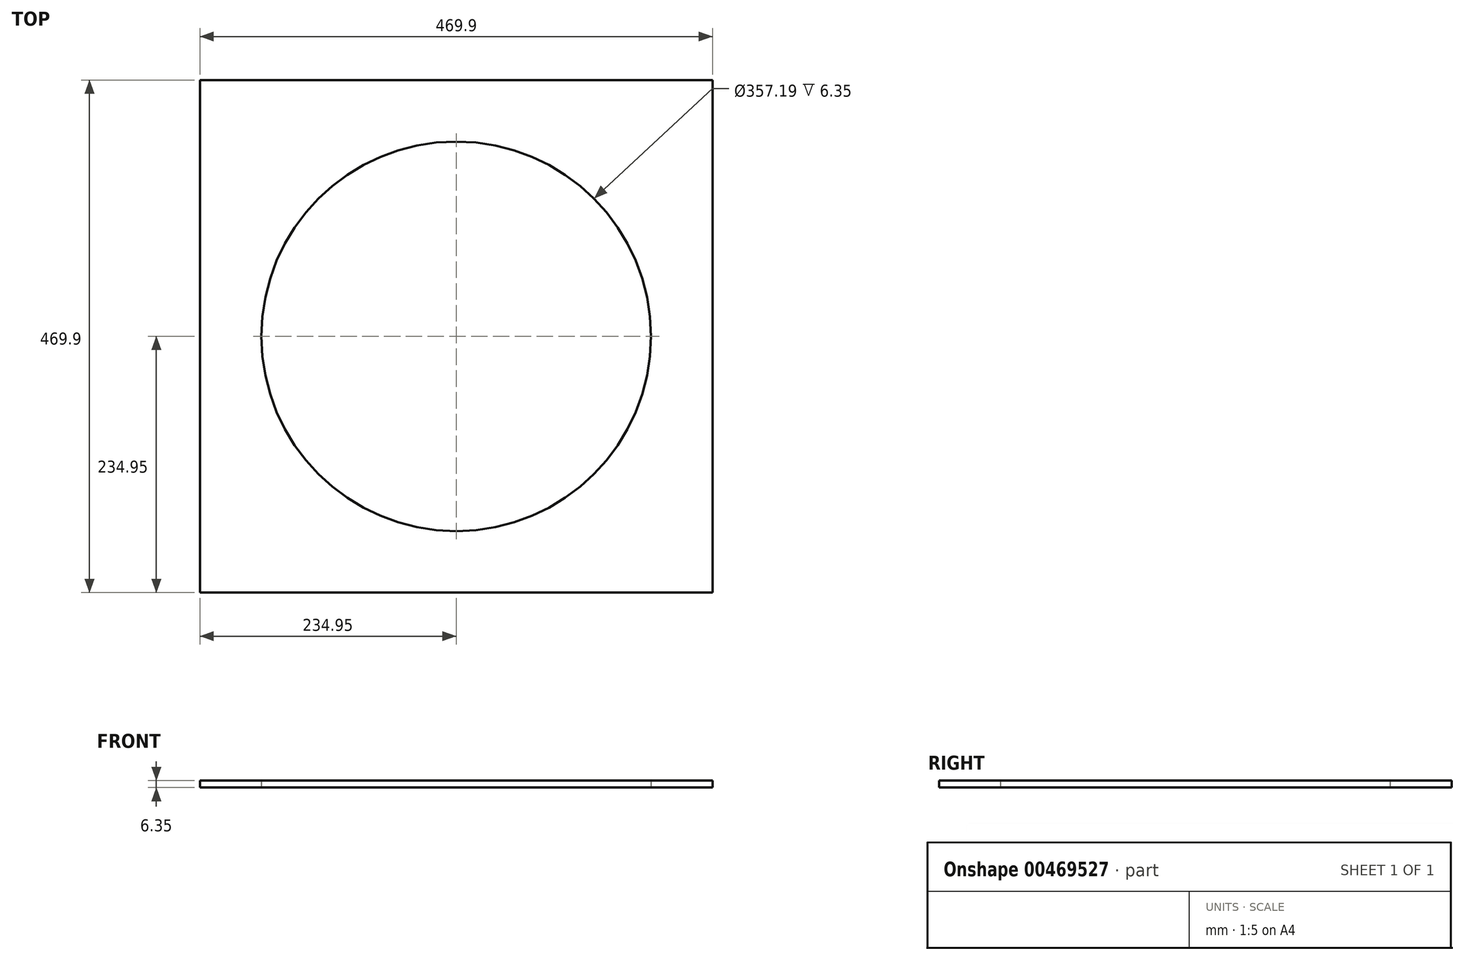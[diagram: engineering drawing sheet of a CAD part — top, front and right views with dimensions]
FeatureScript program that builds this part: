
annotation { "Feature Type Name" : "Feature", "Feature Type Description" : "" }
export const myFeature = defineFeature(function(context is Context, id is Id, definition is map)
    precondition{}
    {
        {
            var Q0;
            Q0=qCreatedBy(makeId("Top.planeOp"),FACE);
            var sketch = newSketch(context, id + "F0", { "sketchPlane" : qUnion([Q0])});
            skCircle(sketch, "E0", {"center": v(0, 0) * mm, "radius": 178.6 * mm});
            skLineSegment(sketch, "E1.bottom", {"start": v(234.95, -234.95) * mm, "end": v(-234.95, -234.95) * mm});
            skLineSegment(sketch, "E1.top", {"start": v(234.95, 234.95) * mm, "end": v(-234.95, 234.95) * mm});
            skLineSegment(sketch, "E1.left", {"start": v(234.95, -234.95) * mm, "end": v(234.95, 234.95) * mm});
            skLineSegment(sketch, "E1.right", {"start": v(-234.95, -234.95) * mm, "end": v(-234.95, 234.95) * mm});
            skSolve(sketch);
        }
        {
            var Q0;
            Q0 = qSketchRegion(id + "F0", true);
            extrude(context, id + "F1", {"entities" : qUnion([Q0]), "depth" : 6.35 * mm, "offsetDistance" : 25.4 * mm});
        }
    });
